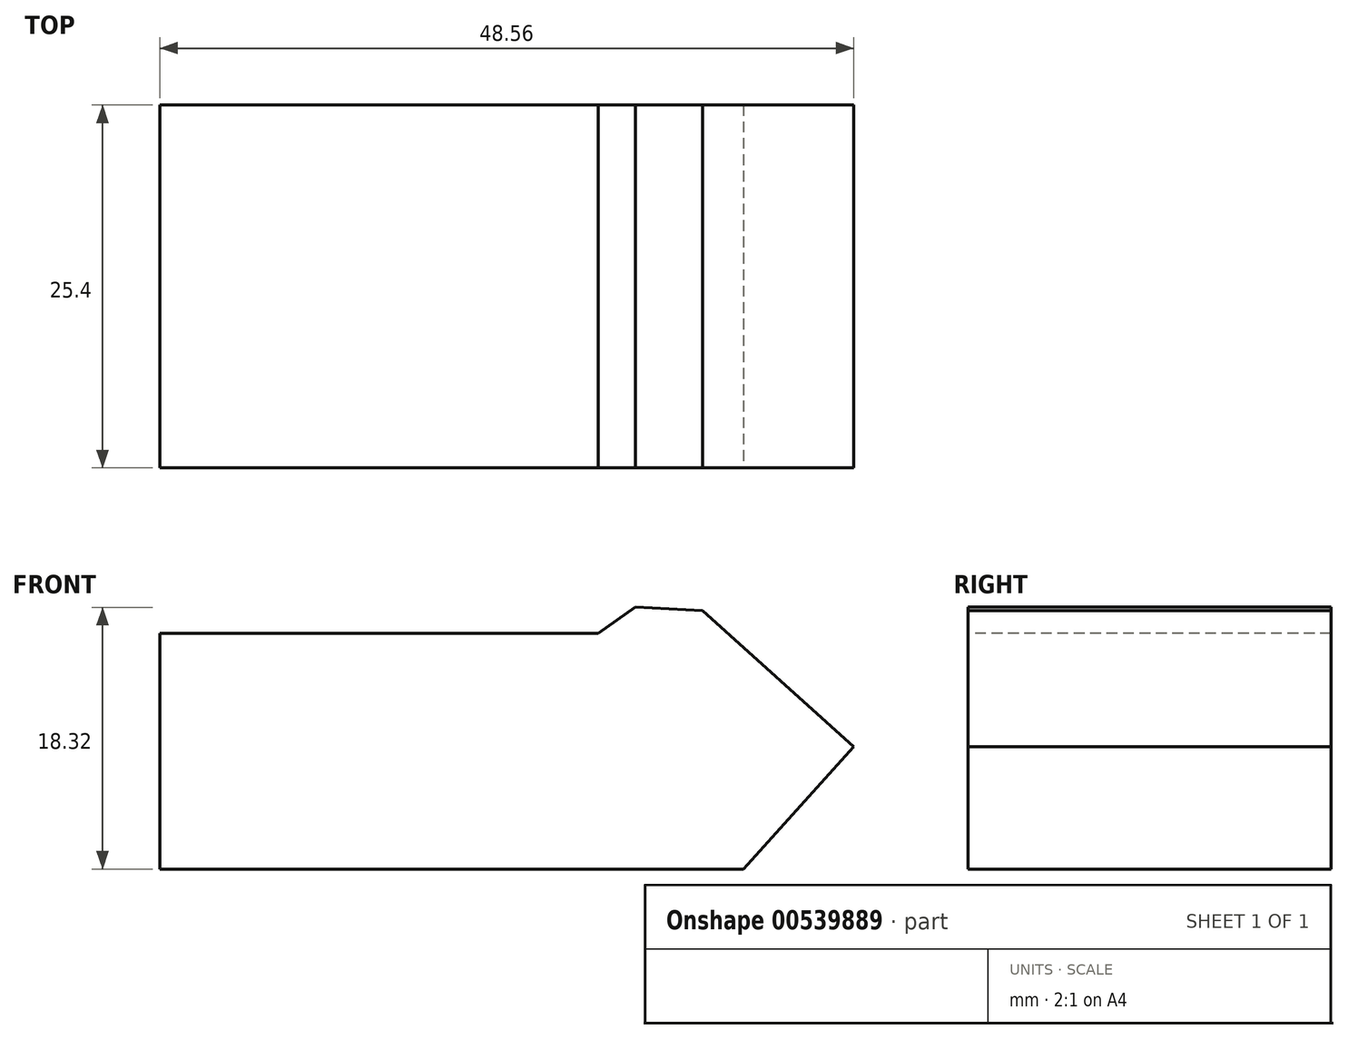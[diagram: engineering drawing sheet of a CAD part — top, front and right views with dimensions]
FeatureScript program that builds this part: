
annotation { "Feature Type Name" : "Feature", "Feature Type Description" : "" }
export const myFeature = defineFeature(function(context is Context, id is Id, definition is map)
    precondition{}
    {
        {
            var Q0;
            Q0=qCreatedBy(makeId("Front.planeOp"),FACE);
            var sketch = newSketch(context, id + "F0", { "sketchPlane" : qUnion([Q0])});
            skLineSegment(sketch, "E0", {"start": v(-1.42, 1.81) * mm, "end": v(3.29, 1.57) * mm});
            skLineSegment(sketch, "E1", {"start": v(3.29, 1.57) * mm, "end": v(13.86, -7.96) * mm});
            skLineSegment(sketch, "E2", {"start": v(13.86, -7.96) * mm, "end": v(6.15, -16.51) * mm});
            skLineSegment(sketch, "E3", {"start": v(6.15, -16.51) * mm, "end": v(-34.7, -16.51) * mm});
            skLineSegment(sketch, "E4", {"start": v(-34.7, -16.51) * mm, "end": v(-34.7, 0) * mm});
            skLineSegment(sketch, "E5", {"start": v(-34.7, 0) * mm, "end": v(-4.03, 0) * mm});
            skLineSegment(sketch, "E6", {"start": v(-4.03, 0) * mm, "end": v(-1.42, 1.81) * mm});
            skSolve(sketch);
        }
        {
            var Q0;
            Q0 = qSketchRegion(id + "F0", true);
            extrude(context, id + "F1", {"entities" : qUnion([Q0]), "oppositeDirection" : true, "depth" : 25.4 * mm, "offsetDistance" : 25.4 * mm});
        }
    });
